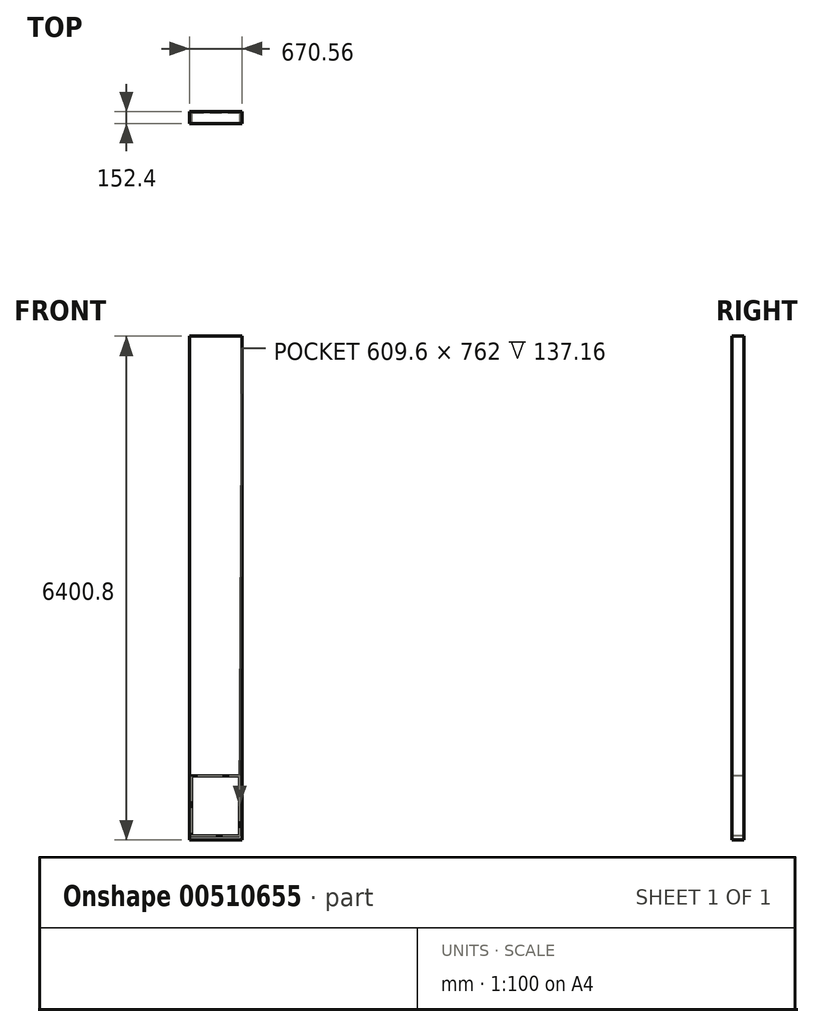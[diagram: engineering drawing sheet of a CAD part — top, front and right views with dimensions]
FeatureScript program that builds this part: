
annotation { "Feature Type Name" : "Feature", "Feature Type Description" : "" }
export const myFeature = defineFeature(function(context is Context, id is Id, definition is map)
    precondition{}
    {
        {
            var Q0;
            Q0=qCreatedBy(makeId("Top.planeOp"),FACE);
            var sketch = newSketch(context, id + "F0", { "sketchPlane" : qUnion([Q0])});
            skLineSegment(sketch, "E0.bottom", {"start": v(-351.1, 33.58) * mm, "end": v(319.45, 33.58) * mm});
            skLineSegment(sketch, "E0.top", {"start": v(-351.1, -118.82) * mm, "end": v(319.45, -118.82) * mm});
            skLineSegment(sketch, "E0.left", {"start": v(-351.1, 33.58) * mm, "end": v(-351.1, -118.82) * mm});
            skLineSegment(sketch, "E0.right", {"start": v(319.45, 33.58) * mm, "end": v(319.45, -118.82) * mm});
            skSolve(sketch);
        }
        {
            var Q0;
            Q0 = qSketchRegion(id + "F0", true);
            extrude(context, id + "F1", {"entities" : qUnion([Q0]), "depth" : 6400.8 * mm, "offsetDistance" : 30.48 * mm});
        }
        {
            var Q0;
            Q0=makeQuery(id+"F1.opExtrude","SWEPT_FACE",FACE,{"disambiguationData":[OSD([sQuery(id+"F0.wireOp",EDGE,"E0.top")])]});
            var sketch = newSketch(context, id + "F2", { "sketchPlane" : qUnion([Q0])});
            skLineSegment(sketch, "E1", {"start": v(-351.1, 6248.4) * mm, "end": v(319.45, 6248.4) * mm});
            skLineSegment(sketch, "E2", {"start": v(-351.1, 5943.6) * mm, "end": v(319.45, 5943.6) * mm});
            skLineSegment(sketch, "E3", {"start": v(-351.1, 5638.8) * mm, "end": v(319.45, 5638.8) * mm});
            skLineSegment(sketch, "E4", {"start": v(-351.1, 5334) * mm, "end": v(319.45, 5334) * mm});
            skLineSegment(sketch, "E5", {"start": v(-351.1, 5029.2) * mm, "end": v(319.45, 5029.2) * mm});
            skLineSegment(sketch, "E6", {"start": v(-351.1, 4724.4) * mm, "end": v(319.45, 4724.4) * mm});
            skLineSegment(sketch, "E7", {"start": v(-351.1, 4419.6) * mm, "end": v(319.45, 4419.6) * mm});
            skLineSegment(sketch, "E8", {"start": v(-351.1, 4114.8) * mm, "end": v(319.45, 4114.8) * mm});
            skLineSegment(sketch, "E9", {"start": v(-351.1, 3810) * mm, "end": v(319.45, 3810) * mm});
            skLineSegment(sketch, "E10", {"start": v(-351.1, 3505.2) * mm, "end": v(319.45, 3505.2) * mm});
            skLineSegment(sketch, "E11", {"start": v(-351.1, 3200.4) * mm, "end": v(319.45, 3200.4) * mm});
            skLineSegment(sketch, "E12", {"start": v(-351.1, 2895.6) * mm, "end": v(319.45, 2895.6) * mm});
            skLineSegment(sketch, "E13", {"start": v(-351.1, 2590.8) * mm, "end": v(319.45, 2590.8) * mm});
            skLineSegment(sketch, "E14", {"start": v(-351.1, 2286) * mm, "end": v(319.45, 2286) * mm});
            skLineSegment(sketch, "E15", {"start": v(-351.1, 1981.2) * mm, "end": v(319.45, 1981.2) * mm});
            skLineSegment(sketch, "E16", {"start": v(-351.1, 1676.4) * mm, "end": v(319.45, 1676.4) * mm});
            skLineSegment(sketch, "E17", {"start": v(-351.1, 1371.6) * mm, "end": v(319.45, 1371.6) * mm});
            skLineSegment(sketch, "E18", {"start": v(-351.1, 1066.8) * mm, "end": v(319.45, 1066.8) * mm});
            skLineSegment(sketch, "E19", {"start": v(-351.1, 762) * mm, "end": v(319.45, 762) * mm});
            skLineSegment(sketch, "E20", {"start": v(0, 762) * mm, "end": v(0, 1066.8) * mm});
            skPoint(sketch, "E20.endSnap0", {"position": v(-15.83, 1066.8) * mm});
            skLineSegment(sketch, "E21", {"start": v(0, 1371.6) * mm, "end": v(0, 1676.4) * mm});
            skLineSegment(sketch, "E22", {"start": v(0, 1981.2) * mm, "end": v(0, 2286) * mm});
            skLineSegment(sketch, "E23", {"start": v(0, 2590.8) * mm, "end": v(0, 2895.6) * mm});
            skLineSegment(sketch, "E24", {"start": v(0, 3200.4) * mm, "end": v(0, 3505.2) * mm});
            skLineSegment(sketch, "E25", {"start": v(0, 3810) * mm, "end": v(0, 4114.8) * mm});
            skPoint(sketch, "E25.startSnap0", {"position": v(-15.83, 3810) * mm});
            skLineSegment(sketch, "E26", {"start": v(0, 4419.6) * mm, "end": v(0, 4724.4) * mm});
            skPoint(sketch, "E26.startSnap0", {"position": v(-15.83, 4419.6) * mm});
            skLineSegment(sketch, "E27", {"start": v(0, 5029.2) * mm, "end": v(0, 5334) * mm});
            skLineSegment(sketch, "E28", {"start": v(0, 5638.8) * mm, "end": v(0, 5943.6) * mm});
            skLineSegment(sketch, "E29", {"start": v(-351.1, 6248.4) * mm, "end": v(-351.1, 762) * mm});
            skLineSegment(sketch, "E30", {"start": v(319.45, 762) * mm, "end": v(319.45, 6248.4) * mm});
            skSolve(sketch);
        }
        {
            var Q0;
            {var subQ0=sQuery(id+"F0.wireOp",EDGE,"E0.top");var subQ1=makeQuery(id+"F1.opExtrude","CAP_EDGE",EDGE,{"disambiguationData":[OSD([subQ0])],"isStart":true});Q0=makeQuery(id+"F2.imprint","IMPRINT",FACE,{"disambiguationData":[TD([[makeQuery(id+"F2.imprint","IMPRINT",EDGE,{"derivedFrom":subQ1}),1.0]])]});}
            var sketch = newSketch(context, id + "F3", { "sketchPlane" : qUnion([Q0])});
            skLineSegment(sketch, "E31.bottom", {"start": v(-320.63, 816.52) * mm, "end": v(288.97, 816.52) * mm});
            skLineSegment(sketch, "E31.top", {"start": v(-320.63, 54.52) * mm, "end": v(288.97, 54.52) * mm});
            skLineSegment(sketch, "E31.left", {"start": v(-320.63, 816.52) * mm, "end": v(-320.63, 54.52) * mm});
            skLineSegment(sketch, "E31.right", {"start": v(288.97, 816.52) * mm, "end": v(288.97, 54.52) * mm});
            skSolve(sketch);
        }
        {
            var Q0;
            Q0 = qSketchRegion(id + "F3", true);
            extrude(context, id + "F4", {"entities" : qUnion([Q0]), "operationType" : NewBodyOperationType.REMOVE, "oppositeDirection" : true, "depth" : 137.16 * mm, "offsetDistance" : 30.48 * mm});
        }
    });
